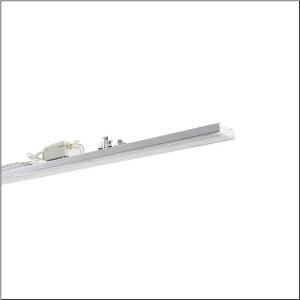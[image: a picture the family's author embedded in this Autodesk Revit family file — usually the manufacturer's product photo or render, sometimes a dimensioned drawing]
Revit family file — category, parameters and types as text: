
# Revit family: licross_r__21_recessed_mo_52tl12cn49xg_563f
name_source: partatom
category: Lighting Fixtures
units: mm (PartAtom-declared; Revit-internal decimal feet)

## family parameters
Cut with Voids When Loaded = No
Host = Face
Light Source = No
Part Type = Normal
Room Calculation Point = No
Round Connector Dimension = Use Diameter
Shared = No

## types (1)
- --- (1 x LED, 9260 lm, 49.9 W, 4000K)
    Apparent Load = 50 VA
    CIE Flux Codes = 72 92 99 100 100
    Color Rendering = 80
    Color Temperature = 4000K
    Default Elevation = 1800 mm
    Description = Licross® 21 Recessed MO, luminaire insert, of sheet steel, galvanised, coil coated, white, length: 1.500mm, width: 66mm, height: 67mm, LED rated luminous flux: 9.260lm, light colour: 840, control gear: ON/OFF Multilumen, CLOi, control gear: ECG Multilumen, with plug, 3-pole, with phase selection, mains connection: 220..240V, AC, 50/60Hz, start of lifetime: 50W, end of service life: 61W, halogen-free wiring, primary optical cover: cover, of PMMA, light emission: direct distribution, primary light characteristic: symmetric, protection rating (complete): IP40, insulation class (complete): insulation class I (protective earthing), certification: CE, ENEC, VDE, UKCA, protection symbol: D if used in an environment without relevant dust loads with corresponding accessories, impact resistance: IK06, permissible ambient temperature for indoor applications: -35..+40°C, corresponds to IFS (International Featured Standards) requirements for safety and quality in the food industry, reducing of maximum allowable ambient temperature of 5°C with ceiling mounting, LABS conformity tested according to VDMA 24364:2018-05, packaging unit: 1 piece
    Height = 58 mm
    Lamp = 1 x LED
    Lamp Light Flux = 9260 lm
    Lamp Power = 49.9 W
    Lamp count = 1
    Length = 1500 mm
    Luminous efficacy = 186 lm/W
    Manufacturer = Siteco
    ModVariant = No
    Model = 52TL12CN49XG
    Mounting Place = Ceiling
    Mounting Type = Pendant
    Number of Poles = 1
    OnlyDefault = Yes
    Power Factor = 1
    Product Name = Licross® 21 Recessed MO
    Product group = luminaire insert
    ProductGroupID = 901
    Protection Class = Protection class I
    Protection Degree = IP 40
    RLX_Detail_Level = 1
    RLX_Emergency_Light_Flux = 0 lm
    RLX_Emergency_Type = 0
    RLX_Emergency_Type_DB = No
    RlxData = <blob elided: 22313 chars, md5=91097215>
    Socket = socket
    Standby Power = 0 W
    System Light Flux = 9260 lm
    System Power = 50 W
    Type Comments = factory setting: luminous flux: 100 % | (A | C | E) | 116 mA
    Type Image = l_1296930.jpg
    URL = http://relux.com
    VarID = @adj_040737
    Voltage = 0 V
    Weight = 0.00 kg
    Width = 66 mm

## geometry (parser evidence)
native form markers: Blend x4, Sweep x9
no freeform markers — native parametric forms only
